# Revit family: Omni Panel
name_source: partatom
category: Plumbing Fixtures
revit_build: Autodesk Revit 2017 (Build: 20160225_1515(x64)
units: mm (PartAtom-declared; Revit-internal decimal feet)

## family parameters
Cut with Voids When Loaded = No
Host = Face
Part Type = Normal
Room Calculation Point = No
Round Connector Dimension = Use Diameter
Shared = No

## types (10) — shared parameters
Default Elevation = 48 "
Description = Omni Panel
Inlet Connector = 0.5 "
Manufacturer = Sioux Chief Manufacturing
Pipe Radius = 0.25 "
URL = www.siouxchief.com

## per-type parameters (varying)
| type | 1807 Visibility | 1960 Visibility | CPVC Visibility | Connector Diameter | MIP Visibility | Male Sweat in Visibility | Outlet Diameter |
| 698-A11-CR | No | No | Yes | 0.38 " | No | No | 0.56 " |
| 698-A11-MR | No | No | No | 0.38 " | Yes | No | 0.56 " |
| 698-A11-PR | No | No | No | 0.38 " | No | Yes | 0.56 " |
| 698-A11-WR | No | Yes | No | 0.38 " | No | No | 0.56 " |
| 698-A11-XR | Yes | No | No | 0.38 " | No | No | 0.56 " |
| 698-A33-CR | No | No | Yes | 0.75 " | No | No | 0.9 " |
| 698-A33-MR | No | No | No | 0.75 " | Yes | No | 0.9 " |
| 698-A33-PR | No | No | No | 0.75 " | No | Yes | 0.9 " |
| 698-A33-WR | No | Yes | No | 0.75 " | No | No | 0.9 " |
| 698-A33-XR | Yes | No | No | 0.75 " | No | No | 0.9 " |

note: column(s) folded — value = type name in every type: Model

## geometry (parser evidence)
native form markers: Sweep x14
no freeform markers — native parametric forms only
